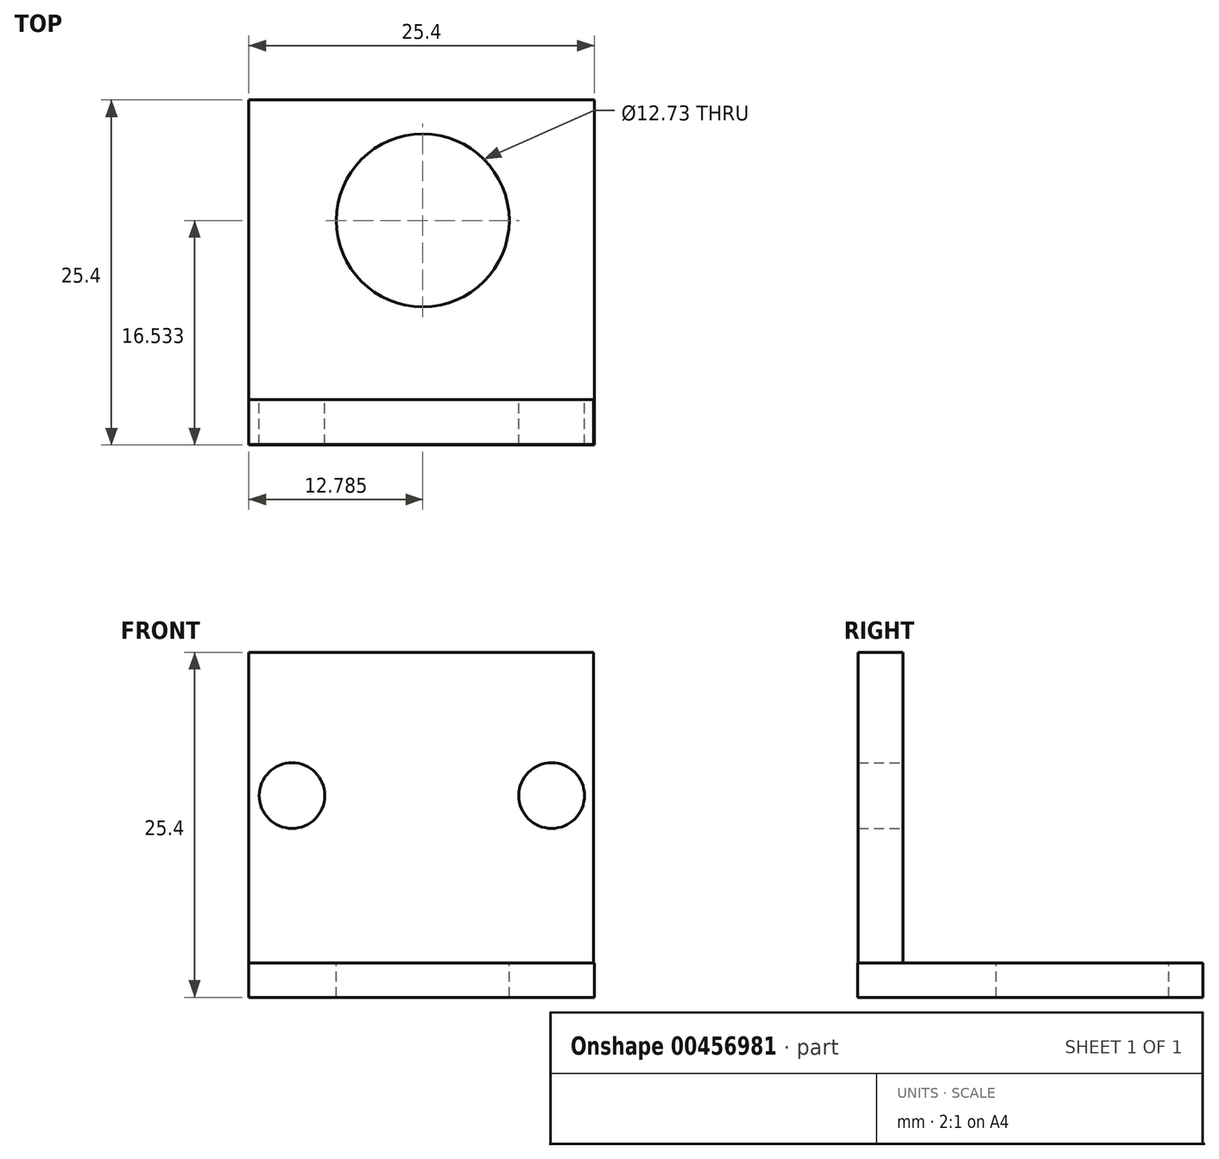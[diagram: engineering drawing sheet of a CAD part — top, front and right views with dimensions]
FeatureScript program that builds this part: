
annotation { "Feature Type Name" : "Feature", "Feature Type Description" : "" }
export const myFeature = defineFeature(function(context is Context, id is Id, definition is map)
    precondition{}
    {
        {
            var Q0;
            Q0=qCreatedBy(makeId("Top.planeOp"),FACE);
            var sketch = newSketch(context, id + "F0", { "sketchPlane" : qUnion([Q0])});
            skLineSegment(sketch, "E0.bottom", {"start": v(0, 0) * mm, "end": v(25.4, 0) * mm});
            skLineSegment(sketch, "E0.top", {"start": v(0, -25.4) * mm, "end": v(25.4, -25.4) * mm});
            skLineSegment(sketch, "E0.left", {"start": v(0, 0) * mm, "end": v(0, -25.4) * mm});
            skLineSegment(sketch, "E0.right", {"start": v(25.4, 0) * mm, "end": v(25.4, -25.4) * mm});
            skSolve(sketch);
        }
        {
            var Q0;
            Q0 = qSketchRegion(id + "F0", true);
            extrude(context, id + "F1", {"entities" : qUnion([Q0]), "depth" : 2.54 * mm});
        }
        {
            var Q0;
            Q0=qCreatedBy(makeId("Top.planeOp"),FACE);
            var sketch = newSketch(context, id + "F2", { "sketchPlane" : qUnion([Q0])});
            skCircle(sketch, "E1", {"center": v(12.79, -8.87) * mm, "radius": 6.36 * mm});
            skSolve(sketch);
        }
        {
            var Q0;
            Q0 = qSketchRegion(id + "F2", true);
            var Q1;
            Q1=sQuery(id+"F2.wireOp",EDGE,"E1");
            extrude(context, id + "F3", {"entities" : qUnion([Q0]), "operationType" : NewBodyOperationType.REMOVE, "surfaceEntities" : qUnion([Q1]), "oppositeDirection" : true, "depth" : 25.4 * mm, "hasSecondDirection" : true, "secondDirectionOppositeDirection" : false, "secondDirectionDepth" : 25.4 * mm});
        }
        {
            var Q0;
            Q0=qCreatedBy(makeId("Top.planeOp"),FACE);
            var sketch = newSketch(context, id + "F4", { "sketchPlane" : qUnion([Q0])});
            skLineSegment(sketch, "E2.bottom", {"start": v(0, -22.06) * mm, "end": v(25.36, -22.06) * mm});
            skLineSegment(sketch, "E2.top", {"start": v(0, -25.36) * mm, "end": v(25.36, -25.36) * mm});
            skLineSegment(sketch, "E2.left", {"start": v(0, -22.06) * mm, "end": v(0, -25.36) * mm});
            skLineSegment(sketch, "E2.right", {"start": v(25.36, -22.06) * mm, "end": v(25.36, -25.36) * mm});
            skSolve(sketch);
        }
        {
            var Q0;
            Q0 = qSketchRegion(id + "F4", true);
            extrude(context, id + "F5", {"entities" : qUnion([Q0]), "operationType" : NewBodyOperationType.ADD, "depth" : 25.4 * mm});
        }
        {
            var Q0;
            Q0=qCreatedBy(makeId("Front.planeOp"),FACE);
            var sketch = newSketch(context, id + "F6", { "sketchPlane" : qUnion([Q0])});
            skCircle(sketch, "E3", {"center": v(22.27, 14.85) * mm, "radius": 2.41 * mm});
            skCircle(sketch, "E4", {"center": v(3.17, 14.85) * mm, "radius": 2.41 * mm});
            skSolve(sketch);
        }
        {
            var Q0;
            Q0 = qSketchRegion(id + "F6", true);
            extrude(context, id + "F7", {"entities" : qUnion([Q0]), "operationType" : NewBodyOperationType.REMOVE, "depth" : 52.07 * mm});
        }
    });
